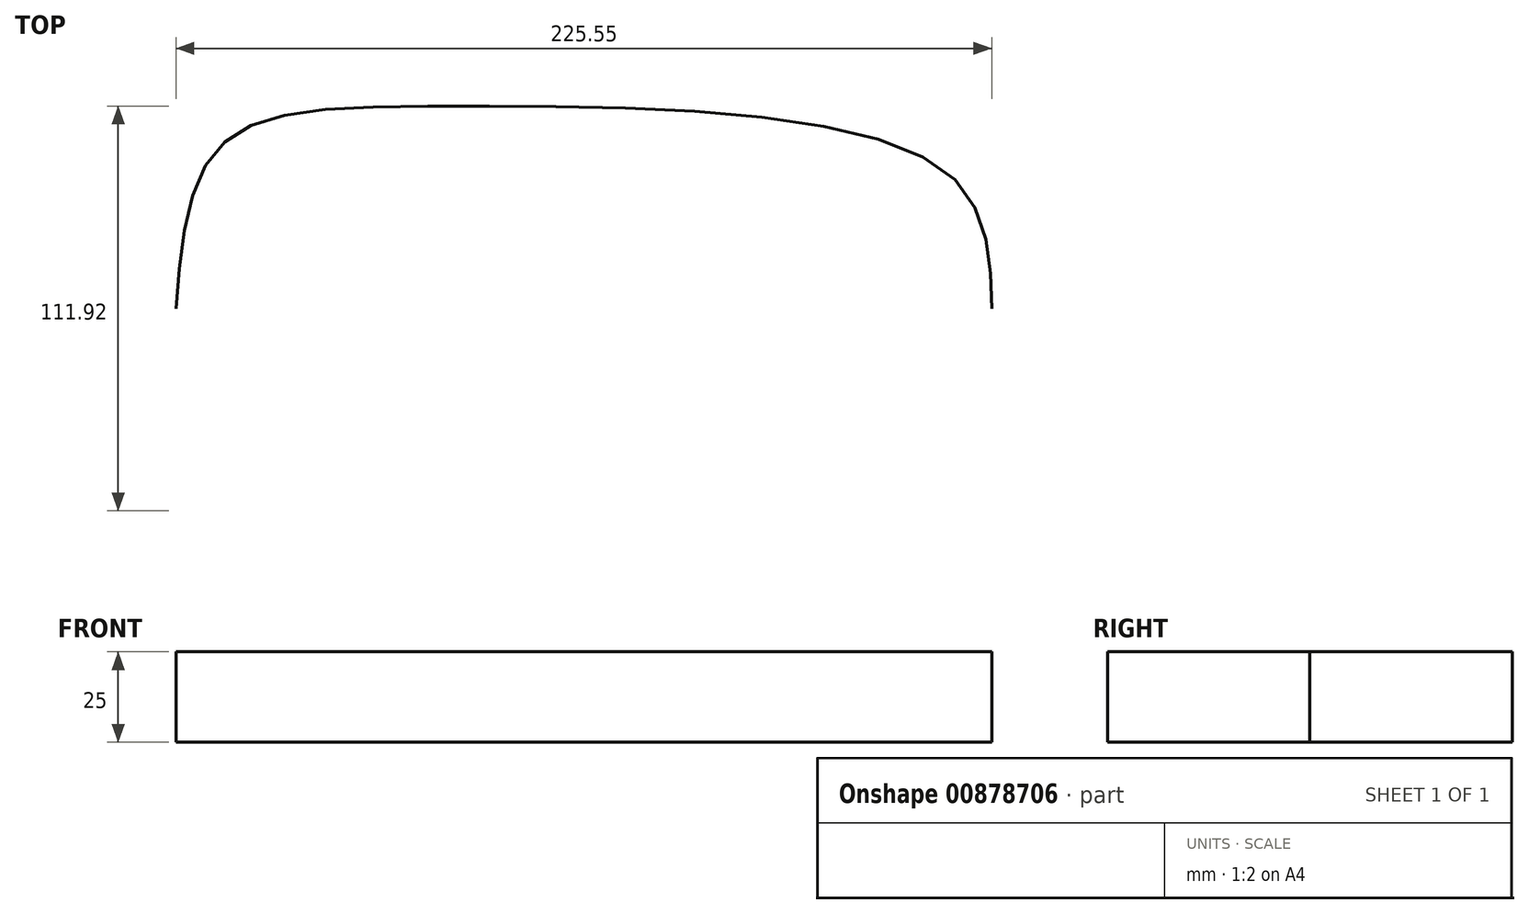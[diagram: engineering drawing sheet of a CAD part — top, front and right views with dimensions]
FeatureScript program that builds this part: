
annotation { "Feature Type Name" : "Feature", "Feature Type Description" : "" }
export const myFeature = defineFeature(function(context is Context, id is Id, definition is map)
    precondition{}
    {
        {
            var Q0;
            Q0=qCreatedBy(makeId("Top.planeOp"),FACE);
            var sketch = newSketch(context, id + "F0", { "sketchPlane" : qUnion([Q0])});
            skFitSpline(sketch, "E0", {"points": [v(-128.79, 0) * mm, v(-116.94, 44.54) * mm, v(-53.75, 55.95) * mm, v(82.71, 38.83) * mm, v(96.76, 0) * mm], "startDerivative": vector(20.4, 255) * mm, "endDerivative": vector(6.4, -225.87) * mm});
            skFitSpline(sketch, "E1.MirrorCS", {"points": [v(-128.79, 0) * mm, v(-116.94, -44.54) * mm, v(-53.75, -55.95) * mm, v(82.71, -38.83) * mm, v(96.76, 0) * mm], "startDerivative": vector(20.4, -255) * mm, "endDerivative": vector(6.4, 225.87) * mm});
            skSolve(sketch);
        }
        {
            var Q0;
            Q0=makeQuery(id+"F0.imprint","IMPRINT",FACE,{"disambiguationData":[TD([[makeQuery(id+"F0.imprint","IMPRINT",EDGE,{"derivedFrom":sQuery(id+"F0.wireOp",EDGE,"E0")}),-1.0]])]});
            extrude(context, id + "F1", {"entities" : qUnion([Q0]), "depth" : 25 * mm, "offsetDistance" : 25 * mm});
        }
    });
